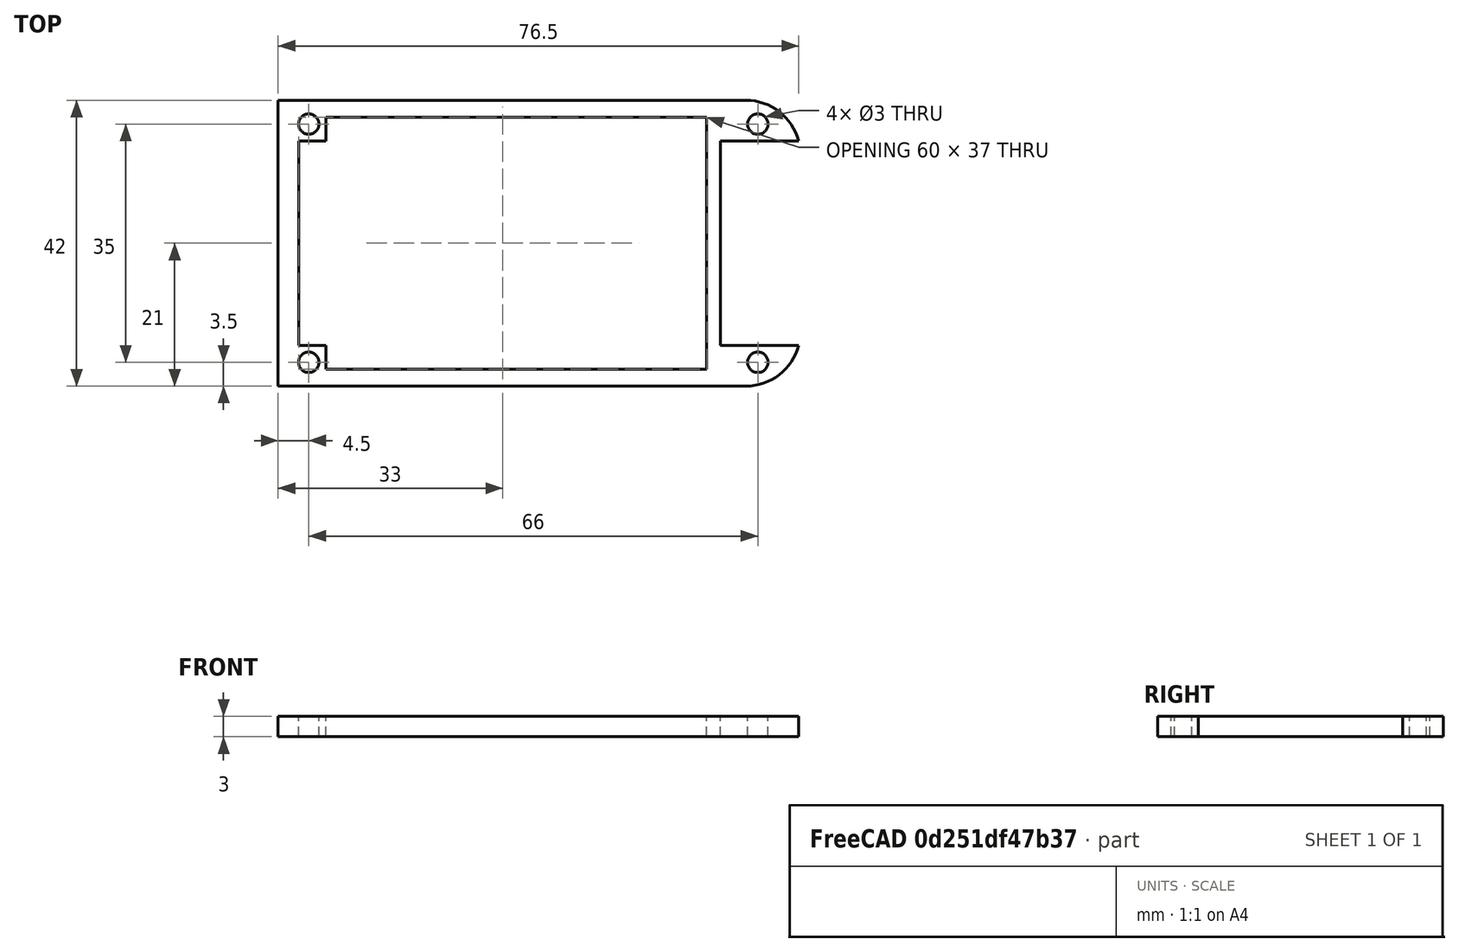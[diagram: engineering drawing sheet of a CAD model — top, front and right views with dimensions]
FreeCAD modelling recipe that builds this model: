
FCSTD DOCUMENT  (FreeCAD 0.18R4 (GitTag))
Label: Adapterplatte
License: All rights reserved
LicenseURL: http://en.wikipedia.org/wiki/All_rights_reserved
objects: Part::Box×5, Part::Cylinder×4, Part::Fillet×1, Part::MultiFuse×1, Part::Cut×1
note: 12 computed .brp shape members not serialized (recipe doc carries the construction recipe); baked Part::Feature solids carry a one-line shape summary decoded from their .brp

FEATURE [Part::Box] Box116  label="Würfel110"
  AttacherType = Attacher::AttachEngine3D
  Height = 6
  Length = 56
  Placement = pos=(-38,-18.5,13) rot=(0,0,1;0rad)
  Width = 37
FEATURE [Part::Box] Box097  label="Base001"
  AttacherType = Attacher::AttachEngine3D
  Height = 3
  Length = 100
  Placement = pos=(-68.25,-21,14) rot=(0,0,1;0rad)
  Width = 42
FEATURE [Part::Fillet] Fillet082
  Base = -> Box097
  Edges = 4 edges r=8: [Edge1,Edge3,Edge5,Edge7]
FEATURE [Part::Box] Box131  label="Würfel121"
  AttacherType = Attacher::AttachEngine3D
  Height = 6
  Length = 12
  Placement = pos=(20,-15,13) rot=(0,0,1;0rad)
  Width = 30
FEATURE [Part::Box] Box130  label="Würfel120"
  AttacherType = Attacher::AttachEngine3D
  Height = 6
  Length = 60
  Placement = pos=(-42,-15,13) rot=(0,0,1;0rad)
  Width = 30
FEATURE [Part::Cylinder] Cylinder223  label="Zylinder223"
  Angle = 360
  AttacherType = Attacher::AttachEngine3D
  Height = 12
  Placement = pos=(25.5,-17.5,8) rot=(0,0,1;0rad)
  Radius = 1.5
FEATURE [Part::Cylinder] Cylinder221  label="Zylinder221"
  Angle = 360
  AttacherType = Attacher::AttachEngine3D
  Height = 12
  Placement = pos=(-40.5,17.5,8) rot=(0,0,1;0rad)
  Radius = 1.5
FEATURE [Part::Cylinder] Cylinder222  label="Zylinder222"
  Angle = 360
  AttacherType = Attacher::AttachEngine3D
  Height = 12
  Placement = pos=(-40.5,-17.5,8) rot=(0,0,1;0rad)
  Radius = 1.5
FEATURE [Part::Cylinder] Cylinder224  label="Zylinder224"
  Angle = 360
  AttacherType = Attacher::AttachEngine3D
  Height = 12
  Placement = pos=(25.5,17.5,8) rot=(0,0,1;0rad)
  Radius = 1.5
FEATURE [Part::Box] Box134  label="Würfel124"
  AttacherType = Attacher::AttachEngine3D
  Height = 6
  Length = 25
  Placement = pos=(-70,-22.5,13) rot=(0,0,1;0rad)
  Width = 45
FEATURE [Part::MultiFuse] Fusion142
  Shapes = -> [Box134,Box116,Box130,Cylinder224,Box131,Cylinder222,Cylinder221,Cylinder223]
FEATURE [Part::Cut] Cut097
  Base = -> Fillet082
  Tool = -> Fusion142
